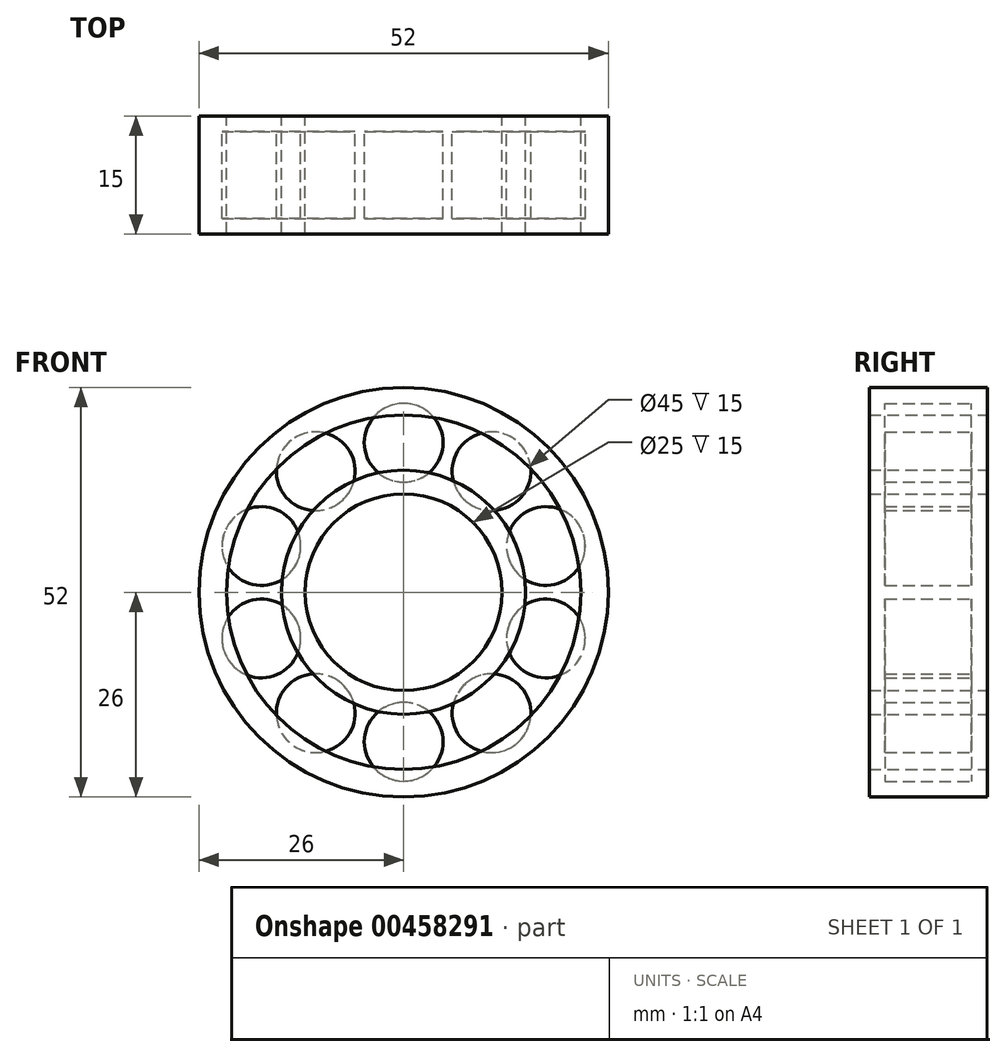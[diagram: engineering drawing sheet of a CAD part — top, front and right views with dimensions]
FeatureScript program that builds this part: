
annotation { "Feature Type Name" : "Feature", "Feature Type Description" : "" }
export const myFeature = defineFeature(function(context is Context, id is Id, definition is map)
    precondition{}
    {
        {
            var Q0;
            Q0=qCreatedBy(makeId("Front.planeOp"),FACE);
            var sketch = newSketch(context, id + "F0", { "sketchPlane" : qUnion([Q0])});
            skCircle(sketch, "E0", {"center": v(0, 0) * mm, "radius": 22.5 * mm});
            skCircle(sketch, "E1", {"center": v(0, 0) * mm, "radius": 26 * mm});
            skCircle(sketch, "E2", {"center": v(0, 0) * mm, "radius": 12.5 * mm});
            skCircle(sketch, "E3", {"center": v(0, 0) * mm, "radius": 15.5 * mm});
            skSolve(sketch);
        }
        {
            var Q0;
            Q0=makeQuery(id+"F0.imprint","IMPRINT",FACE,{"disambiguationData":[TD([[makeQuery(id+"F0.imprint","IMPRINT",EDGE,{"derivedFrom":sQuery(id+"F0.wireOp",EDGE,"E0")}),-1.0]])]});
            var Q1;
            Q1=makeQuery(id+"F0.imprint","IMPRINT",FACE,{"disambiguationData":[TD([[makeQuery(id+"F0.imprint","IMPRINT",EDGE,{"derivedFrom":sQuery(id+"F0.wireOp",EDGE,"E2")}),-1.0]])]});
            extrude(context, id + "F1", {"entities" : qUnion([Q0, Q1]), "depth" : 15 * mm});
        }
        {
            var Q0;
            Q0=qCreatedBy(makeId("Front.planeOp"),FACE);
            cPlane(context, id + "F2", {"entities" : qUnion([Q0]), "cplaneType" : CPlaneType.OFFSET, "offset" : 7.5 * mm, "width" : 150 * mm, "height" : 150 * mm});
        }
        {
            var Q0;
            Q0=qCreatedBy(id+"F2.planeOp",FACE);
            var sketch = newSketch(context, id + "F3", { "sketchPlane" : qUnion([Q0])});
            skCircle(sketch, "E4", {"center": v(0, 0) * mm, "radius": 19 * mm});
            skCircle(sketch, "E5", {"center": v(0, 19) * mm, "radius": 5 * mm});
            skSolve(sketch);
        }
        {
            var Q0;
            {var subQ0=sQuery(id+"F3.wireOp",EDGE,"E5");var subQ1=sQuery(id+"F3.wireOp",EDGE,"E4");var subQ2=makeQuery(id+"F3.imprint","INTERSECT",VERTEX,{"disambiguationData":[OD(0.0)],"derivedFrom":[subQ1,subQ0]});Q0=makeQuery(id+"F3.imprint","IMPRINT",FACE,{"disambiguationData":[TD([[makeQuery(id+"F3.imprint","IMPRINT",EDGE,{"disambiguationData":[TD([[subQ2,1.0]])],"derivedFrom":subQ1}),1.0]])]});}
            var Q1;
            {var subQ0=sQuery(id+"F3.wireOp",EDGE,"E5");var subQ1=sQuery(id+"F3.wireOp",EDGE,"E4");var subQ2=makeQuery(id+"F3.imprint","INTERSECT",VERTEX,{"disambiguationData":[OD(0.0)],"derivedFrom":[subQ1,subQ0]});Q1=makeQuery(id+"F3.imprint","IMPRINT",FACE,{"disambiguationData":[TD([[makeQuery(id+"F3.imprint","IMPRINT",EDGE,{"disambiguationData":[TD([[subQ2,1.0]])],"derivedFrom":subQ1}),-1.0]])]});}
            var Q2;
            Q2=sQuery(id+"F3.wireOp",EDGE,"E5");
            extrude(context, id + "F4", {"entities" : qUnion([Q0, Q1]), "surfaceEntities" : qUnion([Q2]), "depth" : 11 * mm, "symmetric" : true});
        }
        {
            var Q0;
            Q0=makeQuery(id+"F4.opExtrude","SWEPT_BODY",BODY,{"disambiguationData":[OSD([sQuery(id+"F3.wireOp",EDGE,"E5")])]});
            var Q1;
            Q1=makeQuery(id+"F1.opExtrude","CAP_EDGE",EDGE,{"disambiguationData":[OSD([sQuery(id+"F0.wireOp",EDGE,"E2")])],"isStart":false});
            circularPattern(context, id + "F5", {"entities" : qUnion([Q0]), "axis" : qUnion([Q1]), "angle" : 360 * degree, "instanceCount" : 10, "equalSpace" : true});
        }
    });
